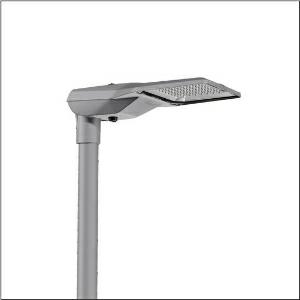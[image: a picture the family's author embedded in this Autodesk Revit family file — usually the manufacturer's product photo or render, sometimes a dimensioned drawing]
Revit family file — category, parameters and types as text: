
# Revit family: streetlight_sl_21_midi___pc-l_5xe3f43t08mb_dba8
name_source: partatom
category: Lighting Fixtures
units: mm (PartAtom-declared; Revit-internal decimal feet)

## family parameters
Cut with Voids When Loaded = No
Host = Face
Light Source = No
Part Type = Normal
Room Calculation Point = No
Round Connector Dimension = Use Diameter
Shared = No

## types (1)
- --- (1 x LED, 19200 lm, 147 W, 4000K)
    Apparent Load = 147 VA
    CIE Flux Codes = 38 78 98 100 100
    Color Rendering = 70
    Color Temperature = 4000K
    Default Elevation = 1800 mm
    Description = Streetlight SL 21 midi, mast luminaire, primary light control with lens, of PMMA, primary optical cover: cover, of toughened safety glass, transparent, light distribution: PC-L, light emission: direct distribution, primary light characteristic: asymmetric, left, installation type: side-entry, post-top, LED, High Power LED, rated luminous flux: 19.200lm, luminous efficacy: 131lm/W, light colour: 740, colour temperature: 4000K, control gear: D4i, control: overheat protection, constant luminous flux control, time-dependent luminous flux control, flexible luminous flux parameterisation, pre-setting: logarithmic dimming characteristic, mains connection: 230..240V, AC, 50/60Hz, start of lifetime: 147W, end of service life: 155W, reduction: 65W, luminaire housing, of diecast aluminium, powder-coated, SITECO metallic grey (DB 702S), corrosivity category C5 high according to DIN EN ISO 12944, please order mast flange separately, inclination adjustable: 0°, 5°, 10°, 15°, sealing non-destructively replaceable, multi-level sealing system, length: 644mm, width: 335mm, height: 110mm, mast flange for spigot size: 42mm (side-entry): 5XC10008XM4, 60/48mm (side-entry/post-top): 5XC10108XM2, 76/60mm (side-entry/post-top): 5XC10108XM1, mounting height: 4..8m, Smart Interface below and above, protection rating (complete): IP66, insulation class (complete): insulation class II (safety insulation), certification: CE, ENEC, ENEC+, VDE, impact resistance: IK10, permissible operating ambient temperature for outdoor applications: -40..+50°C, standard-compliant lighting for roads and squares, packaging unit: 1 piece

Light Distribution: PC-L
    Height = 111 mm
    Lamp = 1 x LED
    Lamp Light Flux = 19200 lm
    Lamp Power = 147 W
    Lamp count = 1
    Length = 644 mm
    Luminous efficacy = 131 lm/W
    Manufacturer = Siteco
    ModVariant = No
    Model = 5XE3F43T08MB
    Number of Poles = 1
    OnlyDefault = Yes
    Power Factor = 1
    Product Name = Streetlight SL 21 midi | PC-L
    Product group = mast luminaire | pylon top
    ProductGroupID = 6100
    Protection Class = Protection class II
    Protection Degree = IP 66
    RLX_Detail_Level = 1
    RLX_Emergency_Light_Flux = 0 lm
    RLX_Emergency_Type = 0
    RLX_Emergency_Type_DB = No
    RlxData = <blob elided: 29653 chars, md5=d3980e1f>
    Socket = socket
    Standby Power = 0 W
    System Light Flux = 19200 lm
    System Power = 147 W
    Type Comments = factory setting: luminous flux: 100 % | dim-lin: 254 | 750 mA
    Type Image = l_1004304.jpg
    URL = http://relux.com
    VarID = @adj_071965
    Voltage = 0 V
    Weight = 0.00 kg
    Width = 336 mm

## geometry (parser evidence)
native form markers: Blend x4, Sweep x10
no freeform markers — native parametric forms only
